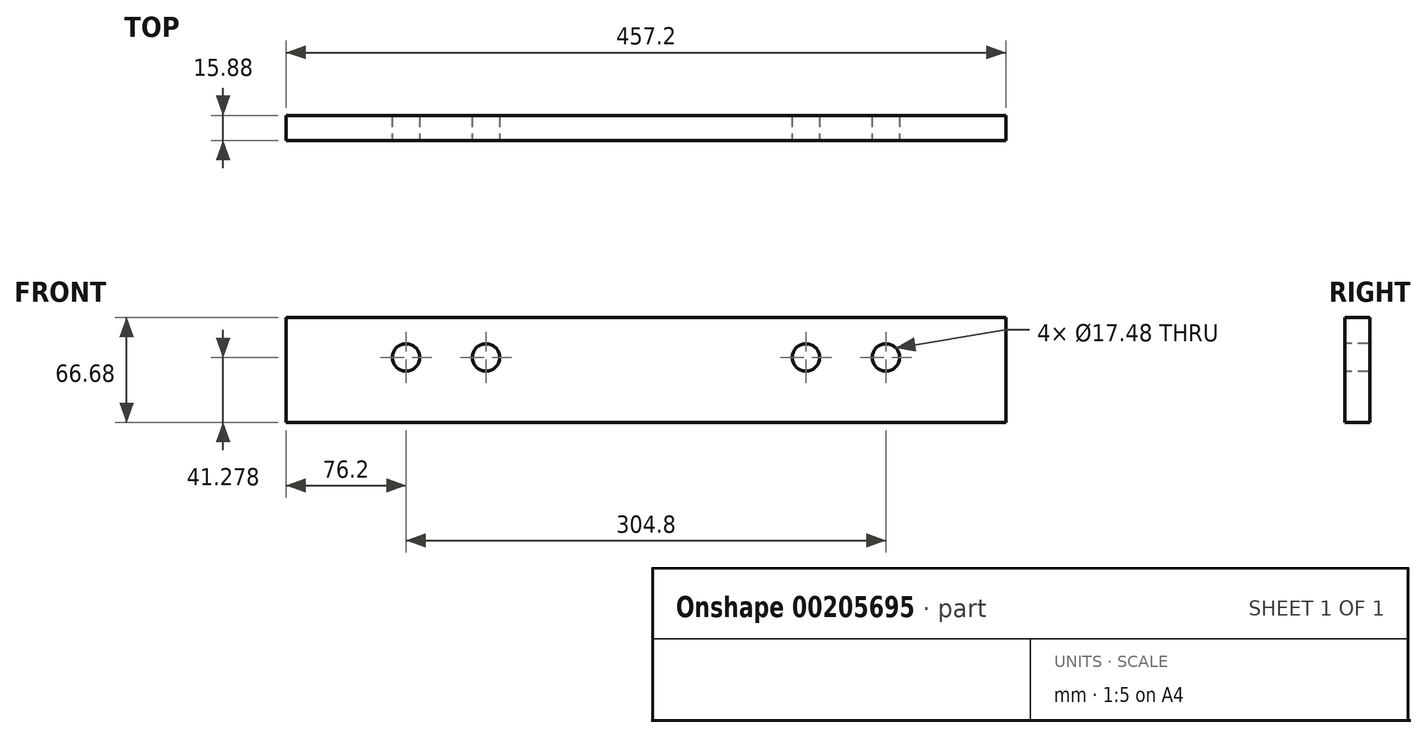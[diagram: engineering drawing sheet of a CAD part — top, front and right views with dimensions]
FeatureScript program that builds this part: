
annotation { "Feature Type Name" : "Feature", "Feature Type Description" : "" }
export const myFeature = defineFeature(function(context is Context, id is Id, definition is map)
    precondition{}
    {
        {
            var Q0;
            Q0=qCreatedBy(makeId("Front.planeOp"),FACE);
            var sketch = newSketch(context, id + "F0", { "sketchPlane" : qUnion([Q0])});
            skLineSegment(sketch, "E0.bottom", {"start": v(228.6, -33.34) * mm, "end": v(-228.6, -33.34) * mm});
            skLineSegment(sketch, "E0.top", {"start": v(228.6, 33.34) * mm, "end": v(-228.6, 33.34) * mm});
            skLineSegment(sketch, "E0.left", {"start": v(228.6, -33.34) * mm, "end": v(228.6, 33.34) * mm});
            skLineSegment(sketch, "E0.right", {"start": v(-228.6, -33.34) * mm, "end": v(-228.6, 33.34) * mm});
            skPoint(sketch, "E0.middle", {"position": v(0, 0) * mm});
            skSolve(sketch);
        }
        {
            var Q0;
            Q0=makeQuery(id+"F0.imprint","IMPRINT",FACE,{"disambiguationData":[TD([[makeQuery(id+"F0.imprint","IMPRINT",EDGE,{"derivedFrom":sQuery(id+"F0.wireOp",EDGE,"E0.bottom")}),-1.0]])]});
            extrude(context, id + "F1", {"entities" : qUnion([Q0]), "depth" : 15.88 * mm});
        }
        {
            var Q0;
            Q0=makeQuery(id+"F1.opExtrude","CAP_FACE",FACE,{"disambiguationData":[OSD([sQuery(id+"F0.wireOp",EDGE,"E0.bottom"),sQuery(id+"F0.wireOp",EDGE,"E0.top"),sQuery(id+"F0.wireOp",EDGE,"E0.left"),sQuery(id+"F0.wireOp",EDGE,"E0.right")])],"isStart":false});
            var sketch = newSketch(context, id + "F2", { "sketchPlane" : qUnion([Q0])});
            skLineSegment(sketch, "E1", {"start": v(0, 33.34) * mm, "end": v(0, -33.34) * mm, "construction": true});
            skLineSegment(sketch, "E2", {"start": v(-228.6, 7.94) * mm, "end": v(228.6, 7.94) * mm, "construction": true});
            skLineSegment(sketch, "E3", {"start": v(-152.4, 33.34) * mm, "end": v(-152.4, -33.34) * mm, "construction": true});
            skLineSegment(sketch, "E4", {"start": v(-101.6, 33.34) * mm, "end": v(-101.6, -33.34) * mm, "construction": true});
            skLineSegment(sketch, "E5", {"start": v(101.6, 33.34) * mm, "end": v(101.6, -33.34) * mm, "construction": true});
            skLineSegment(sketch, "E6", {"start": v(152.4, 33.34) * mm, "end": v(152.4, -33.34) * mm, "construction": true});
            skCircle(sketch, "E7", {"center": v(-152.4, 7.94) * mm, "radius": 8.74 * mm});
            skCircle(sketch, "E8", {"center": v(-101.6, 7.94) * mm, "radius": 8.74 * mm});
            skCircle(sketch, "E9", {"center": v(101.6, 7.94) * mm, "radius": 8.74 * mm});
            skCircle(sketch, "E10", {"center": v(152.4, 7.94) * mm, "radius": 8.74 * mm});
            skSolve(sketch);
        }
        {
            var Q0;
            Q0=makeQuery(id+"F2.imprint","IMPRINT",FACE,{"disambiguationData":[TD([[makeQuery(id+"F2.imprint","IMPRINT",EDGE,{"derivedFrom":sQuery(id+"F2.wireOp",EDGE,"E7")}),1.0]])]});
            var Q1;
            Q1=makeQuery(id+"F2.imprint","IMPRINT",FACE,{"disambiguationData":[TD([[makeQuery(id+"F2.imprint","IMPRINT",EDGE,{"derivedFrom":sQuery(id+"F2.wireOp",EDGE,"E8")}),1.0]])]});
            var Q2;
            Q2=makeQuery(id+"F2.imprint","IMPRINT",FACE,{"disambiguationData":[TD([[makeQuery(id+"F2.imprint","IMPRINT",EDGE,{"derivedFrom":sQuery(id+"F2.wireOp",EDGE,"E9")}),1.0]])]});
            var Q3;
            Q3=makeQuery(id+"F2.imprint","IMPRINT",FACE,{"disambiguationData":[TD([[makeQuery(id+"F2.imprint","IMPRINT",EDGE,{"derivedFrom":sQuery(id+"F2.wireOp",EDGE,"E10")}),1.0]])]});
            extrude(context, id + "F3", {"entities" : qUnion([Q0, Q1, Q2, Q3]), "operationType" : NewBodyOperationType.REMOVE, "endBound" : BoundingType.THROUGH_ALL, "oppositeDirection" : true, "depth" : 25.4 * mm});
        }
    });
